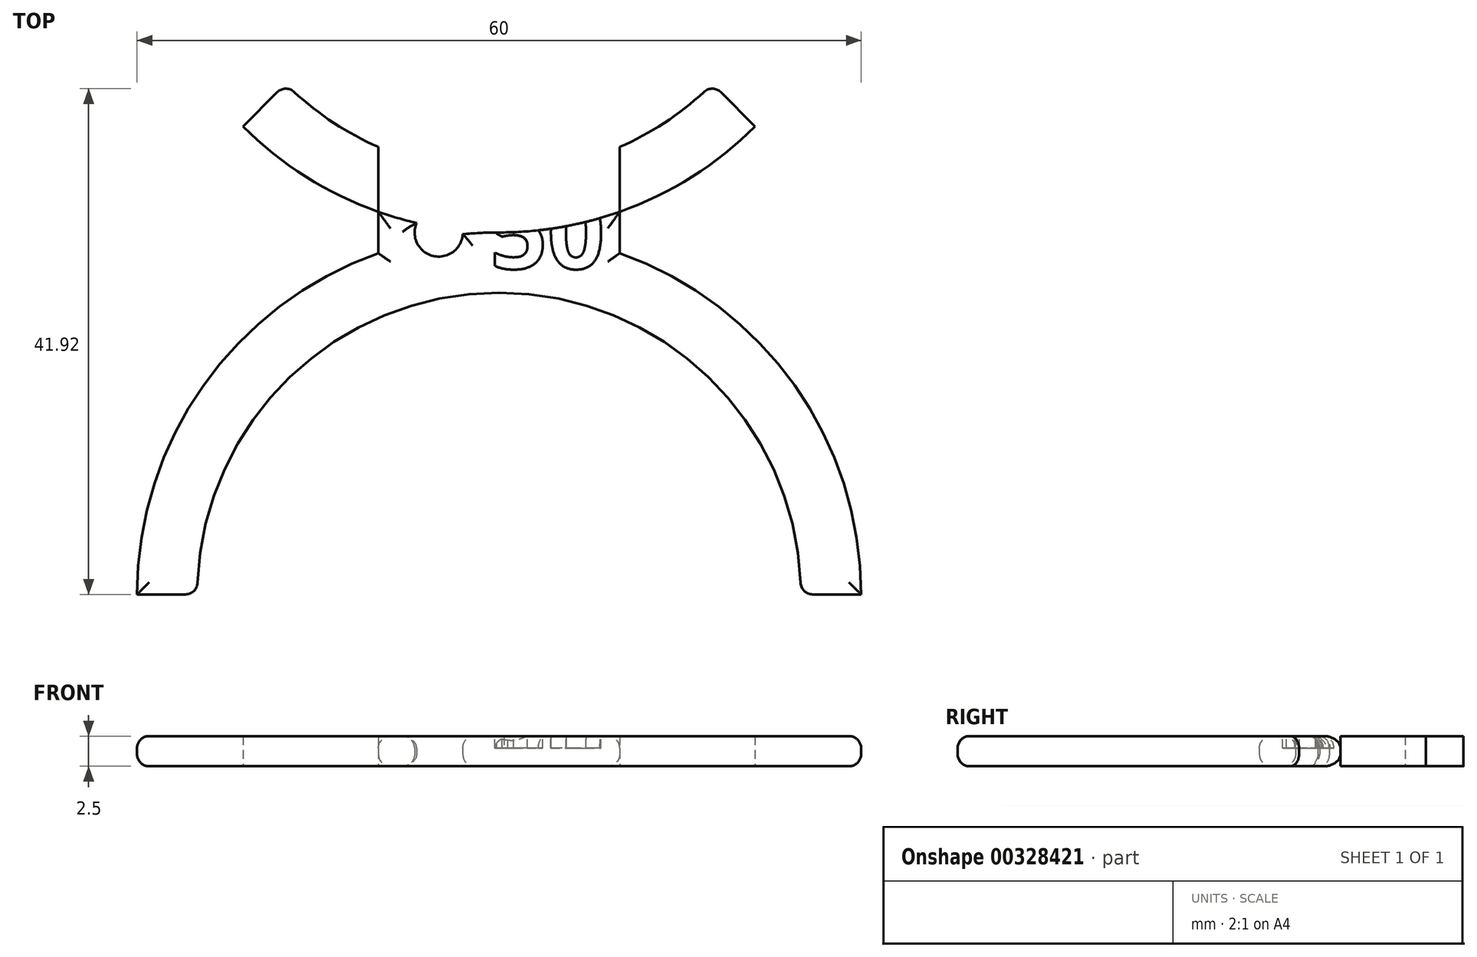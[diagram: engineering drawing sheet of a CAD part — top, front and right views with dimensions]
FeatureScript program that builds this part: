
annotation { "Feature Type Name" : "Feature", "Feature Type Description" : "" }
export const myFeature = defineFeature(function(context is Context, id is Id, definition is map)
    precondition{}
    {
        {
            var Q0;
            Q0=qCreatedBy(makeId("Top.planeOp"),FACE);
            var sketch = newSketch(context, id + "F0", { "sketchPlane" : qUnion([Q0])});
            skLineSegment(sketch, "E0", {"start": v(0, 0) * mm, "end": v(0, -30) * mm, "construction": true});
            skArc(sketch, "E1", {"start": v(-25, -30) * mm, "mid": v(0, -5) * mm, "end": v(25, -30) * mm});
            skArc(sketch, "E2", {"start": v(-30, -30) * mm, "mid": v(0, 0) * mm, "end": v(30, -30) * mm});
            skLineSegment(sketch, "E3", {"start": v(-30, -30) * mm, "end": v(-25, -30) * mm});
            skLineSegment(sketch, "E4", {"start": v(25, -30) * mm, "end": v(30, -30) * mm});
            skLineSegment(sketch, "E5", {"start": v(0, 0) * mm, "end": v(0, 30) * mm});
            skArc(sketch, "E6", {"start": v(30, 30) * mm, "mid": v(0, 0) * mm, "end": v(-30, 30) * mm});
            skArc(sketch, "E7", {"start": v(25, 30) * mm, "mid": v(0, 5) * mm, "end": v(-25, 30) * mm});
            skLineSegment(sketch, "E8", {"start": v(-30, 30) * mm, "end": v(-25, 30) * mm});
            skLineSegment(sketch, "E9", {"start": v(25, 30) * mm, "end": v(30, 30) * mm});
            skLineSegment(sketch, "E10", {"start": v(0, 30) * mm, "end": v(-21.21, 8.79) * mm, "construction": true});
            skLineSegment(sketch, "E11", {"start": v(0, 30) * mm, "end": v(21.21, 8.79) * mm, "construction": true});
            skPoint(sketch, "E12", {"position": v(-17.68, 12.32) * mm});
            skPoint(sketch, "E13", {"position": v(17.68, 12.32) * mm});
            skLineSegment(sketch, "E14", {"start": v(17.68, 12.32) * mm, "end": v(21.21, 8.79) * mm});
            skLineSegment(sketch, "E15", {"start": v(-17.68, 12.32) * mm, "end": v(-21.21, 8.79) * mm});
            skPoint(sketch, "E16", {"position": v(0, 5) * mm});
            skPoint(sketch, "E17", {"position": v(0, -5) * mm});
            skLineSegment(sketch, "E18", {"start": v(-10, 7.09) * mm, "end": v(-10, -7.09) * mm});
            skLineSegment(sketch, "E19", {"start": v(10, 7.09) * mm, "end": v(10, -7.09) * mm});
            skLineSegment(sketch, "E20", {"start": v(0, 0) * mm, "end": v(-10, 0) * mm, "construction": true});
            skCircle(sketch, "E21", {"center": v(-5, 0) * mm, "radius": 2 * mm});
            skSolve(sketch);
        }
        {
            var Q0;
            {var subQ5=sQuery(id+"F0.wireOp",EDGE,"E15");Q0=makeQuery(id+"F0.imprint","IMPRINT",FACE,{"disambiguationData":[TD([[makeQuery(id+"F0.imprint","IMPRINT",EDGE,{"derivedFrom":subQ5}),1.0]])]});}
            var Q1;
            {var subQ5=sQuery(id+"F0.wireOp",EDGE,"E14");Q1=makeQuery(id+"F0.imprint","IMPRINT",FACE,{"disambiguationData":[TD([[makeQuery(id+"F0.imprint","IMPRINT",EDGE,{"derivedFrom":subQ5}),-1.0]])]});}
            var Q2;
            {var subQ0=sQuery(id+"F0.wireOp",EDGE,"E3");Q2=makeQuery(id+"F0.imprint","IMPRINT",FACE,{"disambiguationData":[TD([[makeQuery(id+"F0.imprint","IMPRINT",EDGE,{"derivedFrom":subQ0}),1.0]])]});}
            var Q3;
            {var subQ0=sQuery(id+"F0.wireOp",EDGE,"E4");Q3=makeQuery(id+"F0.imprint","IMPRINT",FACE,{"disambiguationData":[TD([[makeQuery(id+"F0.imprint","IMPRINT",EDGE,{"derivedFrom":subQ0}),1.0]])]});}
            var Q4;
            {var subQ3=sQuery(id+"F0.wireOp",EDGE,"E7");var subQ5=sQuery(id+"F0.wireOp",EDGE,"E18");var subQ6=makeQuery(id+"F0.imprint","INTERSECT",VERTEX,{"derivedFrom":[subQ3,subQ5]});Q4=makeQuery(id+"F0.imprint","IMPRINT",FACE,{"disambiguationData":[TD([[makeQuery(id+"F0.imprint","IMPRINT",EDGE,{"disambiguationData":[TD([[subQ6,1.0]])],"derivedFrom":subQ3}),1.0]])]});}
            var Q5;
            {var subQ3=sQuery(id+"F0.wireOp",EDGE,"E7");var subQ5=sQuery(id+"F0.wireOp",EDGE,"E19");var subQ6=makeQuery(id+"F0.imprint","INTERSECT",VERTEX,{"derivedFrom":[subQ3,subQ5]});Q5=makeQuery(id+"F0.imprint","IMPRINT",FACE,{"disambiguationData":[TD([[makeQuery(id+"F0.imprint","IMPRINT",EDGE,{"disambiguationData":[TD([[subQ6,-1.0]])],"derivedFrom":subQ3}),1.0]])]});}
            var Q6;
            {var subQ1=sQuery(id+"F0.wireOp",EDGE,"E2");var subQ3=sQuery(id+"F0.wireOp",EDGE,"E19");var subQ4=makeQuery(id+"F0.imprint","INTERSECT",VERTEX,{"derivedFrom":[subQ1,subQ3]});Q6=makeQuery(id+"F0.imprint","IMPRINT",FACE,{"disambiguationData":[TD([[makeQuery(id+"F0.imprint","IMPRINT",EDGE,{"disambiguationData":[TD([[subQ4,1.0]])],"derivedFrom":subQ3}),-1.0]])]});}
            var Q7;
            {var subQ0=sQuery(id+"F0.wireOp",EDGE,"E18");var subQ1=sQuery(id+"F0.wireOp",EDGE,"E1");var subQ2=makeQuery(id+"F0.imprint","INTERSECT",VERTEX,{"derivedFrom":[subQ1,subQ0]});Q7=makeQuery(id+"F0.imprint","IMPRINT",FACE,{"disambiguationData":[TD([[makeQuery(id+"F0.imprint","IMPRINT",EDGE,{"disambiguationData":[TD([[subQ2,-1.0]])],"derivedFrom":subQ1}),1.0]])]});}
            var Q8;
            {var subQ1=sQuery(id+"F0.wireOp",EDGE,"E2");var subQ3=sQuery(id+"F0.wireOp",EDGE,"E18");var subQ4=makeQuery(id+"F0.imprint","INTERSECT",VERTEX,{"derivedFrom":[subQ1,subQ3]});Q8=makeQuery(id+"F0.imprint","IMPRINT",FACE,{"disambiguationData":[TD([[makeQuery(id+"F0.imprint","IMPRINT",EDGE,{"disambiguationData":[TD([[subQ4,1.0]])],"derivedFrom":subQ3}),1.0]])]});}
            var Q9;
            {var subQ1=sQuery(id+"F0.wireOp",EDGE,"E2");var subQ3=sQuery(id+"F0.wireOp",EDGE,"E21");var subQ4=makeQuery(id+"F0.imprint","INTERSECT",VERTEX,{"disambiguationData":[OD(1.0)],"derivedFrom":[subQ1,subQ3]});Q9=makeQuery(id+"F0.imprint","IMPRINT",FACE,{"disambiguationData":[TD([[makeQuery(id+"F0.imprint","IMPRINT",EDGE,{"disambiguationData":[TD([[subQ4,-1.0]])],"derivedFrom":subQ3}),-1.0]])]});}
            extrude(context, id + "F1", {"entities" : qUnion([Q0, Q1, Q2, Q3, Q4, Q5, Q6, Q7, Q8, Q9]), "depth" : 2.5 * mm});
        }
        {
            var Q0;
            Q0=makeQuery(id+"F1.opExtrude","CAP_FACE",FACE,{"disambiguationData":[OSD([sQuery(id+"F0.wireOp",EDGE,"E1"),sQuery(id+"F0.wireOp",EDGE,"E2"),sQuery(id+"F0.wireOp",EDGE,"E3"),sQuery(id+"F0.wireOp",EDGE,"E4"),sQuery(id+"F0.wireOp",EDGE,"E6"),sQuery(id+"F0.wireOp",EDGE,"E7"),sQuery(id+"F0.wireOp",EDGE,"E14"),sQuery(id+"F0.wireOp",EDGE,"E15")])],"isStart":false});
            var Q1;
            Q1=makeQuery(id+"F1.opExtrude","CAP_FACE",FACE,{"disambiguationData":[OSD([sQuery(id+"F0.wireOp",EDGE,"E1"),sQuery(id+"F0.wireOp",EDGE,"E2"),sQuery(id+"F0.wireOp",EDGE,"E3"),sQuery(id+"F0.wireOp",EDGE,"E4"),sQuery(id+"F0.wireOp",EDGE,"E6"),sQuery(id+"F0.wireOp",EDGE,"E7"),sQuery(id+"F0.wireOp",EDGE,"E14"),sQuery(id+"F0.wireOp",EDGE,"E15")])],"isStart":true});
            var Q2;
            Q2=makeQuery(id+"F1.opExtrude","SWEPT_EDGE",EDGE,{"disambiguationData":[OSD([sQuery(id+"F0.wireOp",EDGE,"E7"),sQuery(id+"F0.wireOp",EDGE,"E15")])]});
            var Q3;
            Q3=makeQuery(id+"F1.opExtrude","SWEPT_EDGE",EDGE,{"disambiguationData":[OSD([sQuery(id+"F0.wireOp",EDGE,"E7"),sQuery(id+"F0.wireOp",EDGE,"E14")])]});
            var Q4;
            Q4=makeQuery(id+"F1.opExtrude","SWEPT_EDGE",EDGE,{"disambiguationData":[OSD([sQuery(id+"F0.wireOp",EDGE,"E1"),sQuery(id+"F0.wireOp",EDGE,"E4")])]});
            var Q5;
            Q5=makeQuery(id+"F1.opExtrude","SWEPT_EDGE",EDGE,{"disambiguationData":[OSD([sQuery(id+"F0.wireOp",EDGE,"E1"),sQuery(id+"F0.wireOp",EDGE,"E3")])]});
            fillet(context, id + "F2", {"entities" : qUnion([Q0, Q1, Q2, Q3, Q4, Q5]), "radius" : 1 * mm, "tangentPropagation" : true, "allowEdgeOverflow" : false});
        }
        {
            var Q0;
            Q0=makeQuery(id+"F1.opExtrude","CAP_FACE",FACE,{"disambiguationData":[OSD([sQuery(id+"F0.wireOp",EDGE,"E1"),sQuery(id+"F0.wireOp",EDGE,"E2"),sQuery(id+"F0.wireOp",EDGE,"E3"),sQuery(id+"F0.wireOp",EDGE,"E4"),sQuery(id+"F0.wireOp",EDGE,"E6"),sQuery(id+"F0.wireOp",EDGE,"E7"),sQuery(id+"F0.wireOp",EDGE,"E14"),sQuery(id+"F0.wireOp",EDGE,"E15"),sQuery(id+"F0.wireOp",EDGE,"E18"),sQuery(id+"F0.wireOp",EDGE,"E19")])],"isStart":false});
            var sketch = newSketch(context, id + "F3", { "sketchPlane" : qUnion([Q0])});
            skText(sketch, "E22", { "text": "50", "fontName": "OpenSans-Bold.ttf"});
            skPoint(sketch, "E23", {"position": v(4.12, 0) * mm});
            skPoint(sketch, "E24", {"position": v(9, 0) * mm});
            const initialGuessF3  = {"E22": [-0.00076, -0.003, 1, 0, 0.006]};
            skSetInitialGuess(sketch, initialGuessF3);
            skSolve(sketch);
        }
        {
            var Q0;
            Q0 = qSketchRegion(id + "F3", true);
            extrude(context, id + "F4", {"entities" : qUnion([Q0]), "operationType" : NewBodyOperationType.REMOVE, "oppositeDirection" : true, "depth" : 1 * mm});
        }
    });
